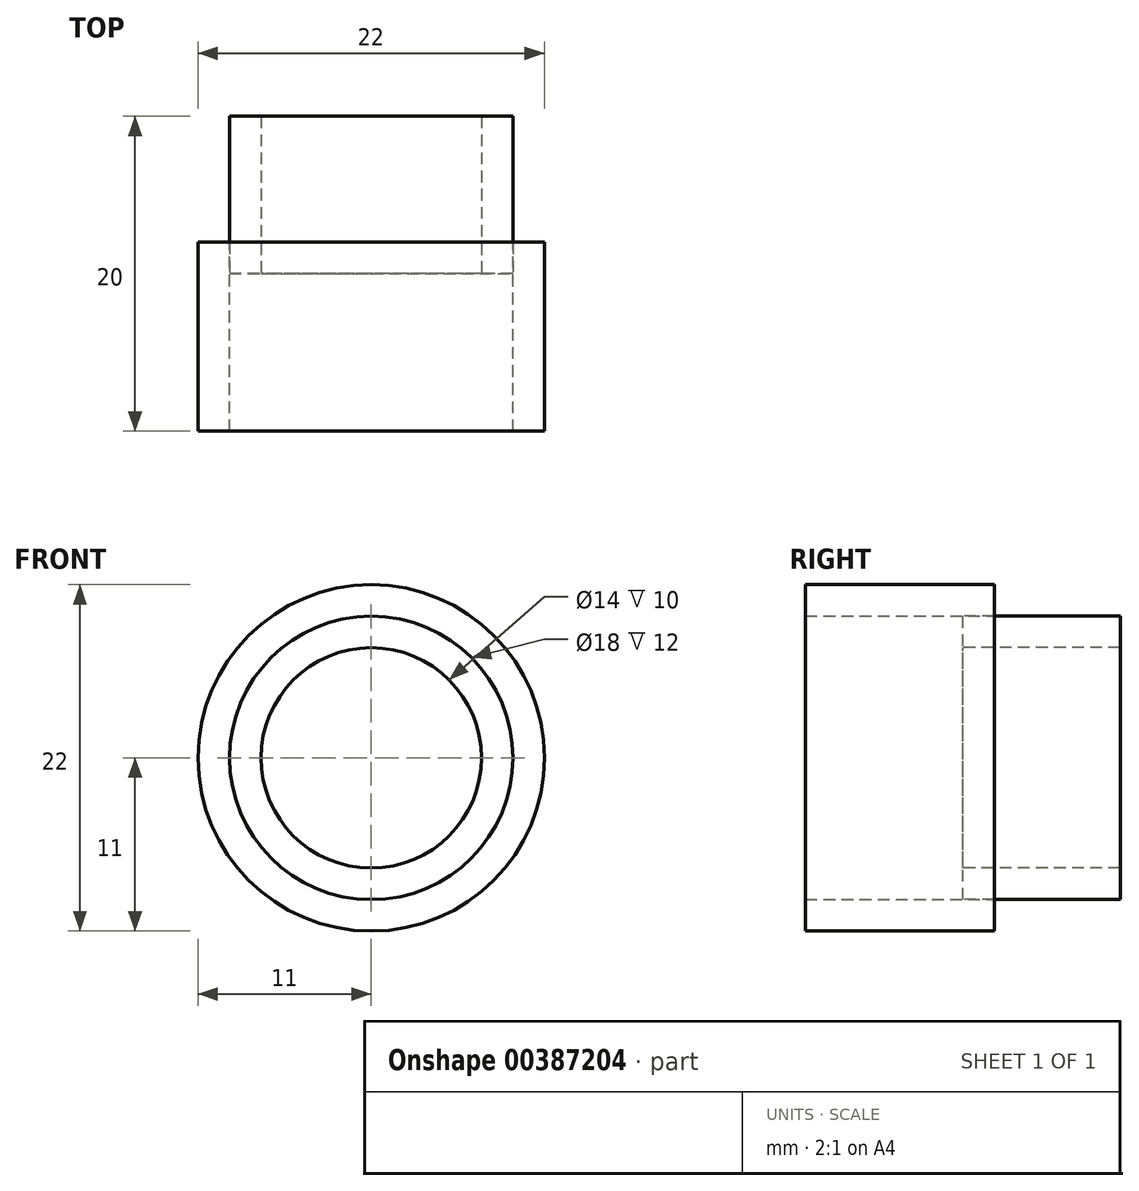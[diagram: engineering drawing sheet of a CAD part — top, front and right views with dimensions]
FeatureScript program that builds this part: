
annotation { "Feature Type Name" : "Feature", "Feature Type Description" : "" }
export const myFeature = defineFeature(function(context is Context, id is Id, definition is map)
    precondition{}
    {
        {
            var Q0;
            Q0=qCreatedBy(makeId("Front.planeOp"),FACE);
            var sketch = newSketch(context, id + "F0", { "sketchPlane" : qUnion([Q0])});
            skCircle(sketch, "E0", {"center": v(0, 0) * mm, "radius": 9 * mm});
            skCircle(sketch, "E1", {"center": v(0, 0) * mm, "radius": 11 * mm});
            skCircle(sketch, "E2", {"center": v(0, 0) * mm, "radius": 7 * mm});
            skSolve(sketch);
        }
        {
            var Q0;
            Q0 = qSketchRegion(id + "F0", true);
            var Q1;
            Q1 = qSketchRegion(id + "F8ts1gaUvf7hsTU_1", true);
            extrude(context, id + "F1", {"entities" : qUnion([Q0, Q1]), "depth" : 12 * mm});
        }
        {
            var Q0;
            Q0=makeQuery(id+"F0.imprint","IMPRINT",FACE,{"disambiguationData":[TD([[makeQuery(id+"F0.imprint","IMPRINT",EDGE,{"derivedFrom":sQuery(id+"F0.wireOp",EDGE,"E0")}),1.0]])]});
            extrude(context, id + "F2", {"entities" : qUnion([Q0]), "flatOperationType" : FlatOperationType.REMOVE, "offsetDistance" : 25 * mm, "depth" : -8 * mm, "hasSecondDirection" : true, "secondDirectionOppositeDirection" : true, "secondDirectionDepth" : -2 * mm, "domain" : OperationDomain.MODEL});
        }
    });
